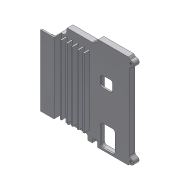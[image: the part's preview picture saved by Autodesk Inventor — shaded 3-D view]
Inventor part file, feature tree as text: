
AUTODESK INVENTOR PART (.ipt)
format: ipt  version: 2014 SP1 (Build 180222100, 222)  size: 803,328 bytes
history: native  units: in
note: dims shown in document units (in); Inventor stores cm internally (conversion verified against a paired STEP export)
features: projected_geometry x19, sketch x11, extrude x8, reference x8, plane x3, hole x3, fillet x1, imported_body x1
ambient origin geometry x8: Origin, YZ Plane, XZ Plane, XY Plane, X Axis, Y Axis, Z Axis, Center Point
bodies: Solid1 (feature_tree)
feature tree (54):
  plane  "Work Plane1"
  extrude  "Extrusion1"  Depth=1.9685in
  extrude  "Extrusion2"  Depth=0.3937in TaperAngle=0.0deg
  plane  "Work Plane2"
  plane  "Work Plane3"
  extrude  "Extrusion3"  Depth=0.0394in
  fillet  "Fillet1"  Radius=0.189in
  extrude  "Extrusion5"  Depth=0.189in
  extrude  "Extrusion6"  Depth=0.063in
  extrude  "Extrusion7"  Depth=0.0039in
  extrude  "Extrusion8"  Depth=0.0591in
  hole  "Hole1"  [1 undecoded]
  hole  "Hole2"  [1 undecoded]
  extrude  "Extrusion9"  Depth=0.0394in TaperAngle=0.0deg
  hole  "Hole3"  [1 undecoded]
  sketch  "Sketch1"  dims[d0=0.0in d2=1.9685in]
  projected_geometry  "Projected Loop1"
  projected_geometry  "Projected Loop2"
  projected_geometry  "Projected Loop3"
  projected_geometry  "Projected Loop4"
  projected_geometry  "Projected Loop5"
  projected_geometry  "Projected Loop6"
  projected_geometry  "Projected Loop7"
  projected_geometry  "Projected Loop8"
  projected_geometry  "Projected Loop9"
  projected_geometry  "Projected Loop10"
  projected_geometry  "Projected Loop11"
  projected_geometry  "Projected Loop12"
  projected_geometry  "Projected Loop13"
  projected_geometry  "Projected Loop14"
  projected_geometry  "Projected Loop15"
  projected_geometry  "Projected Loop16"
  sketch  "Sketch2"  dims[d3=0.3937in d4=0.0in d5=0.3937in d6=0.0in]
  projected_geometry  "Projected Loop17"
  sketch  "Sketch3"  dims[d7=1.9685in d8=0.0394in d10=0.189in]
  reference  "Reference1"
  reference  "Reference2"
  reference  "Reference3"
  reference  "Reference4"
  reference  "Reference5"
  projected_geometry  "Projected Loop18"
  reference  "Reference6"
  sketch  "Sketch5"  dims[d11=0.5512in d12=0.189in]
  sketch  "Sketch6"  dims[d14=0.3543in d15=0.0in d18=0.063in]
  sketch  "Sketch7"  dims[d20=0.0591in d21=0.0039in]
  sketch  "Sketch8"  dims[d22=0.3307in d23=0.0591in]
  sketch  "Sketch9"  dims[d24=1.9685in d26=0.3543in d27=0.0in]
  sketch  "Sketch11"  dims[d28=0.3543in d29=0.0in d30=0.0394in d31=0.0in]
  reference  "Reference7"
  reference  "Reference8"
  sketch  "Sketch12"  dims[d32=0.0394in d33=0.0in]
  projected_geometry  "Projected Loop19"
  sketch  "Sketch13"  dims[d34=0.0617in d35=0.2362in d36=0.1575in d37=0.0787in d38=90.0deg d39=0.1181in d40=0.8108in d41=0.0617in d42=0.2362in d43=0.1575in d44=0.0787in d45=90.0deg d46=0.1181in d47=0.8108in d48=0.0394in d49=0.0in d50=0.0617in d51=0.2362in d52=0.1575in d53=0.0787in d54=90.0deg d55=0.1181in d56=0.8108in]
  imported_body  "Base1"
note: 3 required parameter values undecoded (feature->parameter linkage not recoverable at this tier; creation-order binding heuristic only, values carry confidence <= 0.55)
